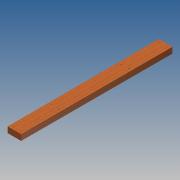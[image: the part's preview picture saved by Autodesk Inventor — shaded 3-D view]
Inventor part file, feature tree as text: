
AUTODESK INVENTOR PART (.ipt)
format: ipt  version: 2014 SP1 (Build 180222100, 222)  size: 116,224 bytes
history: native  units: in
note: dims shown in document units (in); Inventor stores cm internally (conversion verified against a paired STEP export)
features: sketch x4, hole x3, extrude x1
ambient origin geometry x8: Origin, YZ Plane, XZ Plane, XY Plane, X Axis, Y Axis, Z Axis, Center Point
bodies: Solid1 (feature_tree)
feature tree (8):
  extrude  "Extrusion1"  Depth=1.5in
  hole  "Hole1"  [1 undecoded]
  hole  "Hole2"  [1 undecoded]
  hole  "Hole3"  [1 undecoded]
  sketch  "Sketch1"  dims[d0=3.5in d1=1.5in]
  sketch  "Sketch2"  dims[d2=39.0in d3=0.0in d4=0.75in]
  sketch  "Sketch3"  dims[d5=0.75in d6=0.7874in d8=2.0in d9=0.7874in d11=37.5in]
  sketch  "Sketch4"  dims[d14=0.201in d15=0.75in d16=0.385in d17=0.25in d18=0.5635in d19=1.0in d20=0.8108in d21=9.0in d22=0.7874in d24=2.0in d25=0.3937in d27=1.0in d29=0.201in d30=0.75in d31=0.385in d32=0.25in d33=0.5635in d34=1.0in d35=0.8108in d36=8.25in d37=0.5in d38=0.201in d39=0.75in d40=0.385in d41=0.25in d42=0.5635in d43=1.0in d44=0.8108in]
note: 3 required parameter values undecoded (feature->parameter linkage not recoverable at this tier; creation-order binding heuristic only, values carry confidence <= 0.55)
